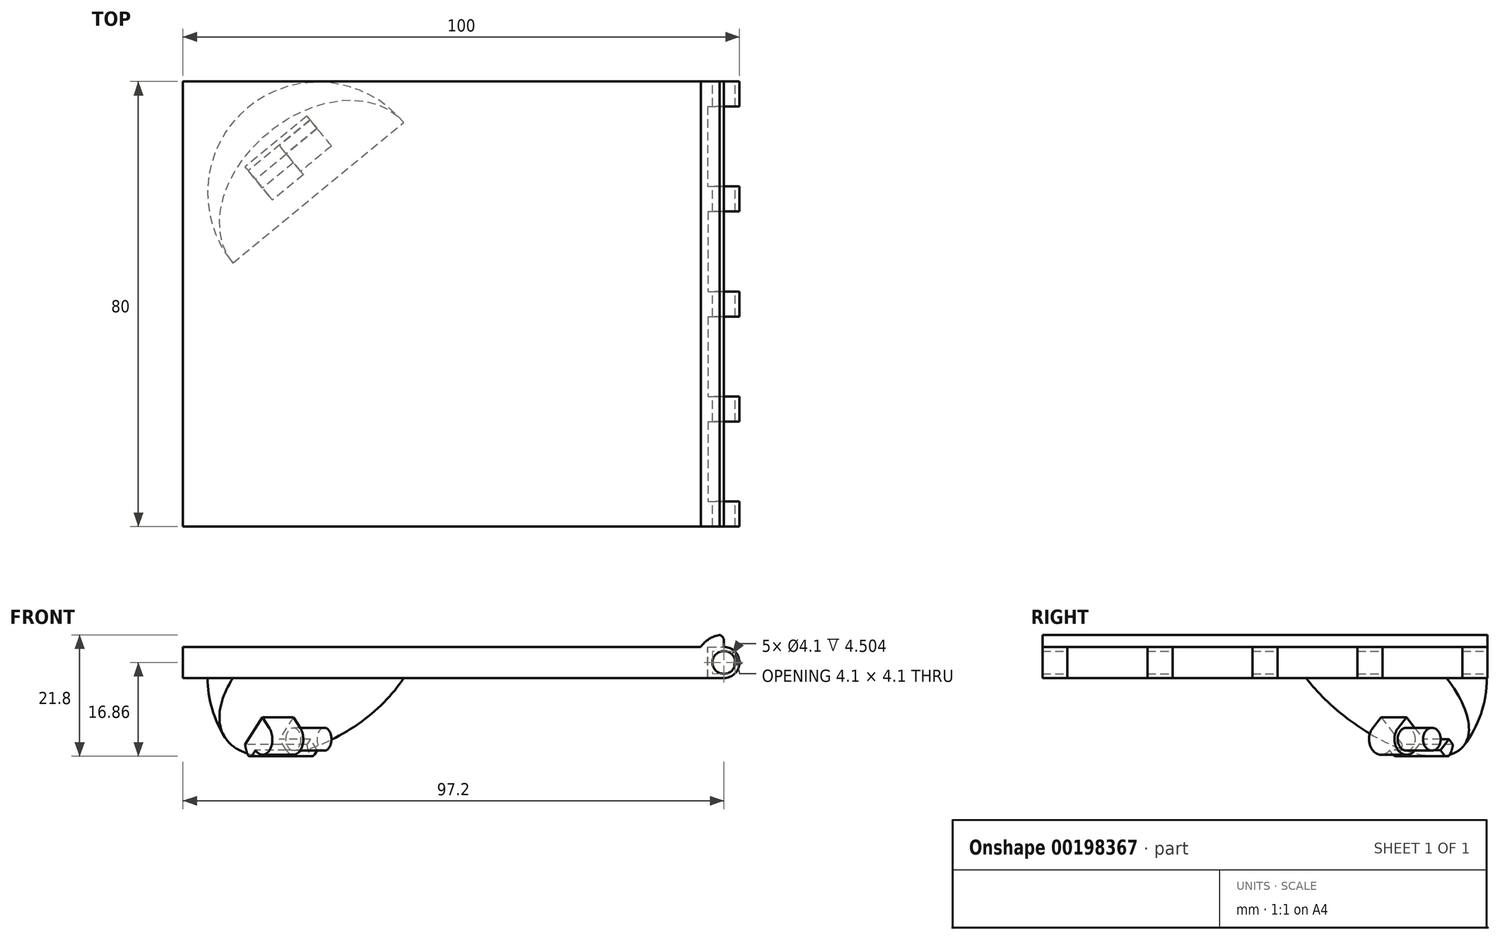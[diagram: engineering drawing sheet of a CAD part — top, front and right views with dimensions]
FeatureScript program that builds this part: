
annotation { "Feature Type Name" : "Feature", "Feature Type Description" : "" }
export const myFeature = defineFeature(function(context is Context, id is Id, definition is map)
    precondition{}
    {
        {
            var Q0;
            Q0=qCreatedBy(makeId("Front.planeOp"),FACE);
            var sketch = newSketch(context, id + "F0", { "sketchPlane" : qUnion([Q0])});
            skLineSegment(sketch, "E0.bottom", {"start": v(0, 0) * mm, "end": v(100, 0) * mm});
            skLineSegment(sketch, "E0.top", {"start": v(0, 5.6) * mm, "end": v(100, 5.6) * mm});
            skLineSegment(sketch, "E0.left", {"start": v(0, 0) * mm, "end": v(0, 5.6) * mm});
            skLineSegment(sketch, "E0.right", {"start": v(100, 0) * mm, "end": v(100, 5.6) * mm});
            skSolve(sketch);
        }
        {
            var Q0;
            Q0=makeQuery(id+"F0.imprint","IMPRINT",FACE,{"disambiguationData":[TD([[makeQuery(id+"F0.imprint","IMPRINT",EDGE,{"derivedFrom":sQuery(id+"F0.wireOp",EDGE,"E0.bottom")}),1.0]])]});
            extrude(context, id + "F1", {"entities" : qUnion([Q0]), "depth" : 80 * mm});
        }
        {
            var Q0;
            Q0=makeQuery(id+"F1.opExtrude","SWEPT_FACE",FACE,{"disambiguationData":[OSD([sQuery(id+"F0.wireOp",EDGE,"E0.top")])]});
            var sketch = newSketch(context, id + "F2", { "sketchPlane" : qUnion([Q0])});
            skLineSegment(sketch, "E1.bottom", {"start": v(100, 0) * mm, "end": v(94.3, 0) * mm, "construction": true});
            skLineSegment(sketch, "E1.top", {"start": v(100, -4.5) * mm, "end": v(94.3, -4.5) * mm, "construction": true});
            skLineSegment(sketch, "E1.left", {"start": v(100, 0) * mm, "end": v(100, -4.5) * mm, "construction": true});
            skLineSegment(sketch, "E1.right", {"start": v(94.3, 0) * mm, "end": v(94.3, -4.5) * mm, "construction": true});
            skLineSegment(sketch, "E2.bottom", {"start": v(94.3, -4.5) * mm, "end": v(100, -4.5) * mm});
            skLineSegment(sketch, "E2.top", {"start": v(94.3, -18.87) * mm, "end": v(100, -18.87) * mm});
            skLineSegment(sketch, "E2.left", {"start": v(94.3, -4.5) * mm, "end": v(94.3, -18.87) * mm});
            skLineSegment(sketch, "E2.right", {"start": v(100, -4.5) * mm, "end": v(100, -18.87) * mm});
            skLineSegment(sketch, "E3.0.1.0", {"start": v(100, -23.38) * mm, "end": v(100, -37.75) * mm});
            skLineSegment(sketch, "E3.0.1.1", {"start": v(100, -18.87) * mm, "end": v(94.3, -18.87) * mm, "construction": true});
            skLineSegment(sketch, "E3.0.1.2", {"start": v(94.3, -23.38) * mm, "end": v(94.3, -37.75) * mm});
            skLineSegment(sketch, "E3.0.1.3", {"start": v(94.3, -37.75) * mm, "end": v(100, -37.75) * mm});
            skLineSegment(sketch, "E3.0.1.4", {"start": v(100, -23.38) * mm, "end": v(94.3, -23.38) * mm, "construction": true});
            skLineSegment(sketch, "E3.0.1.5", {"start": v(100, -18.87) * mm, "end": v(100, -23.38) * mm, "construction": true});
            skLineSegment(sketch, "E3.0.1.6", {"start": v(94.3, -18.87) * mm, "end": v(94.3, -23.38) * mm, "construction": true});
            skLineSegment(sketch, "E3.0.1.7", {"start": v(94.3, -23.38) * mm, "end": v(100, -23.38) * mm});
            skLineSegment(sketch, "E3.0.2.0", {"start": v(100.02, -42.25) * mm, "end": v(100.02, -56.62) * mm});
            skLineSegment(sketch, "E3.0.2.1", {"start": v(100.02, -37.75) * mm, "end": v(94.32, -37.75) * mm, "construction": true});
            skLineSegment(sketch, "E3.0.2.2", {"start": v(94.32, -42.25) * mm, "end": v(94.32, -56.62) * mm});
            skLineSegment(sketch, "E3.0.2.3", {"start": v(94.32, -56.62) * mm, "end": v(100.02, -56.62) * mm});
            skLineSegment(sketch, "E3.0.2.4", {"start": v(100.02, -42.25) * mm, "end": v(94.32, -42.25) * mm, "construction": true});
            skLineSegment(sketch, "E3.0.2.5", {"start": v(100.02, -37.75) * mm, "end": v(100.02, -42.25) * mm, "construction": true});
            skLineSegment(sketch, "E3.0.2.6", {"start": v(94.32, -37.75) * mm, "end": v(94.32, -42.25) * mm, "construction": true});
            skLineSegment(sketch, "E3.0.2.7", {"start": v(94.32, -42.25) * mm, "end": v(100.02, -42.25) * mm});
            skLineSegment(sketch, "E3.0.3.0", {"start": v(100.03, -61.13) * mm, "end": v(100.03, -75.5) * mm});
            skLineSegment(sketch, "E3.0.3.1", {"start": v(100.03, -56.62) * mm, "end": v(94.33, -56.62) * mm, "construction": true});
            skLineSegment(sketch, "E3.0.3.2", {"start": v(94.33, -61.13) * mm, "end": v(94.33, -75.5) * mm});
            skLineSegment(sketch, "E3.0.3.3", {"start": v(94.33, -75.5) * mm, "end": v(100.03, -75.5) * mm});
            skLineSegment(sketch, "E3.0.3.4", {"start": v(100.03, -61.13) * mm, "end": v(94.33, -61.13) * mm, "construction": true});
            skLineSegment(sketch, "E3.0.3.5", {"start": v(100.03, -56.62) * mm, "end": v(100.03, -61.13) * mm, "construction": true});
            skLineSegment(sketch, "E3.0.3.6", {"start": v(94.33, -56.62) * mm, "end": v(94.33, -61.13) * mm, "construction": true});
            skLineSegment(sketch, "E3.0.3.7", {"start": v(94.33, -61.13) * mm, "end": v(100.03, -61.13) * mm});
            skLineSegment(sketch, "E3.direction1", {"start": v(94.3, -18.87) * mm, "end": v(119.7, -18.87) * mm, "construction": true});
            skLineSegment(sketch, "E3.direction2", {"start": v(94.3, -18.87) * mm, "end": v(94.3, -37.75) * mm, "construction": true});
            skSolve(sketch);
        }
        {
            var Q0;
            Q0=makeQuery(id+"F1.opExtrude","CAP_FACE",FACE,{"disambiguationData":[OSD([sQuery(id+"F0.wireOp",EDGE,"E0.bottom"),sQuery(id+"F0.wireOp",EDGE,"E0.top"),sQuery(id+"F0.wireOp",EDGE,"E0.left"),sQuery(id+"F0.wireOp",EDGE,"E0.right")])],"isStart":true});
            var sketch = newSketch(context, id + "F3", { "sketchPlane" : qUnion([Q0])});
            skLineSegment(sketch, "E4.bottom", {"start": v(-100, 5.6) * mm, "end": v(-94.4, 5.6) * mm, "construction": true});
            skLineSegment(sketch, "E4.top", {"start": v(-100, 0) * mm, "end": v(-94.4, 0) * mm, "construction": true});
            skLineSegment(sketch, "E4.left", {"start": v(-100, 5.6) * mm, "end": v(-100, 0) * mm, "construction": true});
            skLineSegment(sketch, "E4.right", {"start": v(-94.4, 5.6) * mm, "end": v(-94.4, 0) * mm, "construction": true});
            skLineSegment(sketch, "E5", {"start": v(-100, 5.6) * mm, "end": v(-94.4, 0) * mm, "construction": true});
            skCircle(sketch, "E6", {"center": v(-97.2, 2.8) * mm, "radius": 2.05 * mm});
            skLineSegment(sketch, "E7", {"start": v(-97.2, 2.8) * mm, "end": v(-97.2, 6.7) * mm, "construction": true});
            skLineSegment(sketch, "E8", {"start": v(-97.2, 6.7) * mm, "end": v(-97.2, 5.6) * mm});
            skCircle(sketch, "E9", {"center": v(-97.2, 6.7) * mm, "radius": 1.1 * mm, "construction": true});
            skArc(sketch, "E10", {"start": v(-96.45, 7.74) * mm, "mid": v(-97.19, 6.52) * mm, "end": v(-96.1, 5.6) * mm});
            skCircle(sketch, "E11", {"center": v(-97.2, 2.8) * mm, "radius": 2.8 * mm});
            skLineSegment(sketch, "E12", {"start": v(-97.2, 0) * mm, "end": v(-93.06, 0) * mm});
            skPoint(sketch, "E13.orphan", {"position": v(-97.2, 7.8) * mm});
            skLineSegment(sketch, "E14", {"start": v(-96.1, 5.6) * mm, "end": v(-93.06, 5.6) * mm});
            skLineSegment(sketch, "E15", {"start": v(-97.2, 5.6) * mm, "end": v(-100, 5.6) * mm});
            skLineSegment(sketch, "E16", {"start": v(-100, 5.6) * mm, "end": v(-100, 0) * mm});
            skLineSegment(sketch, "E17", {"start": v(-100, 0) * mm, "end": v(-97.2, 0) * mm});
            skCircle(sketch, "E18", {"center": v(-94.4, 2.8) * mm, "radius": 2.8 * mm, "construction": true});
            skLineSegment(sketch, "E19", {"start": v(-93.06, 0) * mm, "end": v(-91.6, 0) * mm});
            skArc(sketch, "E20.trimOffspring", {"start": v(-94.4, 2.8) * mm, "mid": v(-93.58, 0.82) * mm, "end": v(-91.6, 0) * mm});
            skArc(sketch, "E21.trimOffspring", {"start": v(-93.06, 5.6) * mm, "mid": v(-94.53, 7.03) * mm, "end": v(-96.45, 7.74) * mm});
            skLineSegment(sketch, "E22", {"start": v(-94.4, 2.8) * mm, "end": v(-94.4, 5.6) * mm});
            skSolve(sketch);
        }
        {
            var Q0;
            {var subQ0=sQuery(id+"F3.wireOp",EDGE,"E15");Q0=makeQuery(id+"F3.imprint","IMPRINT",FACE,{"disambiguationData":[TD([[makeQuery(id+"F3.imprint","IMPRINT",EDGE,{"derivedFrom":subQ0}),1.0]])]});}
            var Q1;
            {var subQ0=sQuery(id+"F3.wireOp",EDGE,"E17");Q1=makeQuery(id+"F3.imprint","IMPRINT",FACE,{"disambiguationData":[TD([[makeQuery(id+"F3.imprint","IMPRINT",EDGE,{"derivedFrom":subQ0}),-1.0]])]});}
            var Q2;
            Q2=makeQuery(id+"F3.imprint","IMPRINT",FACE,{"disambiguationData":[TD([[makeQuery(id+"F3.imprint","IMPRINT",EDGE,{"derivedFrom":sQuery(id+"F3.wireOp",EDGE,"E6")}),1.0]])]});
            extrude(context, id + "F4", {"entities" : qUnion([Q0, Q1, Q2]), "operationType" : NewBodyOperationType.REMOVE, "oppositeDirection" : true, "depth" : 80 * mm});
        }
        {
            var Q0;
            Q0=makeQuery(id+"F2.imprint","IMPRINT",FACE,{"disambiguationData":[TD([[makeQuery(id+"F2.imprint","IMPRINT",EDGE,{"derivedFrom":sQuery(id+"F2.wireOp",EDGE,"E2.bottom")}),-1.0]])]});
            var Q1;
            {var subQ0=sQuery(id+"F2.wireOp",EDGE,"E3.0.1.2");Q1=makeQuery(id+"F2.imprint","IMPRINT",FACE,{"disambiguationData":[TD([[makeQuery(id+"F2.imprint","IMPRINT",EDGE,{"derivedFrom":subQ0}),1.0]])]});}
            var Q2;
            {var subQ0=sQuery(id+"F2.wireOp",EDGE,"E3.0.2.2");Q2=makeQuery(id+"F2.imprint","IMPRINT",FACE,{"disambiguationData":[TD([[makeQuery(id+"F2.imprint","IMPRINT",EDGE,{"derivedFrom":subQ0}),1.0]])]});}
            var Q3;
            {var subQ0=sQuery(id+"F2.wireOp",EDGE,"E3.0.3.2");Q3=makeQuery(id+"F2.imprint","IMPRINT",FACE,{"disambiguationData":[TD([[makeQuery(id+"F2.imprint","IMPRINT",EDGE,{"derivedFrom":subQ0}),1.0]])]});}
            extrude(context, id + "F5", {"entities" : qUnion([Q0, Q1, Q2, Q3]), "operationType" : NewBodyOperationType.REMOVE, "oppositeDirection" : true, "depth" : 5.6 * mm});
        }
        {
            var Q0;
            {var subQ3=sQuery(id+"F3.wireOp",EDGE,"E14");Q0=makeQuery(id+"F3.imprint","IMPRINT",FACE,{"disambiguationData":[TD([[makeQuery(id+"F3.imprint","IMPRINT",EDGE,{"derivedFrom":subQ3}),-1.0]])]});}
            var Q1;
            {var subQ0=sQuery(id+"F3.wireOp",EDGE,"E8");Q1=makeQuery(id+"F3.imprint","IMPRINT",FACE,{"disambiguationData":[TD([[makeQuery(id+"F3.imprint","IMPRINT",EDGE,{"derivedFrom":subQ0}),1.0]])]});}
            extrude(context, id + "F6", {"entities" : qUnion([Q0, Q1]), "operationType" : NewBodyOperationType.ADD, "oppositeDirection" : true, "depth" : 80 * mm});
        }
        {
            var Q0;
            Q0=makeQuery(id+"F1.opExtrude","SWEPT_FACE",FACE,{"disambiguationData":[OSD([sQuery(id+"F0.wireOp",EDGE,"E0.bottom")])]});
            var sketch = newSketch(context, id + "F7", { "sketchPlane" : qUnion([Q0])});
            skLineSegment(sketch, "E23", {"start": v(0, 40) * mm, "end": v(97.2, 39.47) * mm, "construction": true});
            skLineSegment(sketch, "E24", {"start": v(48.6, 0) * mm, "end": v(48.6, 80) * mm, "construction": true});
            skLineSegment(sketch, "E25", {"start": v(0, 40) * mm, "end": v(48.6, 0) * mm, "construction": true});
            skCircle(sketch, "E26", {"center": v(24.3, 20) * mm, "radius": 19.87 * mm});
            skLineSegment(sketch, "E27", {"start": v(8.96, 32.63) * mm, "end": v(39.64, 7.37) * mm});
            skSolve(sketch);
        }
        {
            var Q0;
            {var subQ0=sQuery(id+"F7.wireOp",EDGE,"E27");Q0=makeQuery(id+"F7.imprint","IMPRINT",FACE,{"disambiguationData":[TD([[makeQuery(id+"F7.imprint","IMPRINT",EDGE,{"derivedFrom":subQ0}),-1.0]])]});}
            var Q1;
            Q1=sQuery(id+"F7.wireOp",EDGE,"E27");
            revolve(context, id + "F8", {"operationType" : NewBodyOperationType.ADD, "entities" : qUnion([Q0]), "axis" : qUnion([Q1]), "revolveType" : RevolveType.ONE_DIRECTION, "oppositeDirection" : true, "angle" : 45 * degree});
        }
        {
            var Q0;
            Q0=makeQuery(id+"F8.opRevolve","CAP_FACE",FACE,{"disambiguationData":[OSD([sQuery(id+"F7.wireOp",EDGE,"E26"),sQuery(id+"F7.wireOp",EDGE,"E27")])],"isStart":false});
            var sketch = newSketch(context, id + "F9", { "sketchPlane" : qUnion([Q0])});
            skLineSegment(sketch, "E28", {"start": v(16.22, 15.83) * mm, "end": v(6.22, -1.34) * mm, "construction": true});
            skLineSegment(sketch, "E29", {"start": v(11.22, 7.24) * mm, "end": v(5, 10.86) * mm});
            skLineSegment(sketch, "E30", {"start": v(11.22, 7.24) * mm, "end": v(17.43, 3.63) * mm});
            skLineSegment(sketch, "E31", {"start": v(17.43, 3.63) * mm, "end": v(14.61, -1.2) * mm});
            skLineSegment(sketch, "E32", {"start": v(5, 10.86) * mm, "end": v(2.2, 6.02) * mm});
            skLineSegment(sketch, "E33", {"start": v(14.61, -1.2) * mm, "end": v(2.2, 6.02) * mm});
            skLineSegment(sketch, "E34", {"start": v(11.22, 7.24) * mm, "end": v(8.4, 2.4) * mm});
            skSolve(sketch);
        }
        {
            var Q0;
            Q0=makeQuery(id+"F9.imprint","IMPRINT",FACE,{"disambiguationData":[TD([[makeQuery(id+"F9.imprint","IMPRINT",EDGE,{"derivedFrom":sQuery(id+"F9.wireOp",EDGE,"E29")}),1.0]])]});
            extrude(context, id + "F10", {"entities" : qUnion([Q0]), "operationType" : NewBodyOperationType.ADD, "depth" : 5.6 * mm});
        }
        {
            var Q0;
            Q0=makeQuery(id+"F10.opExtrude","SWEPT_FACE",FACE,{"disambiguationData":[OSD([sQuery(id+"F9.wireOp",EDGE,"E32")])]});
            var sketch = newSketch(context, id + "F11", { "sketchPlane" : qUnion([Q0])});
            skLineSegment(sketch, "E35", {"start": v(23.86, -7.02) * mm, "end": v(23.86, -14.94) * mm, "construction": true});
            skCircle(sketch, "E36", {"center": v(23.86, -10.98) * mm, "radius": 2.05 * mm});
            skArc(sketch, "E37", {"start": v(20.32, -14.52) * mm, "mid": v(27.65, -7.73) * mm, "end": v(19.83, -13.95) * mm});
            skLineSegment(sketch, "E38", {"start": v(23.86, -10.98) * mm, "end": v(21.88, -12.96) * mm, "construction": true});
            skLineSegment(sketch, "E39", {"start": v(18.86, -10.98) * mm, "end": v(23.86, -10.98) * mm, "construction": true});
            skLineSegment(sketch, "E40", {"start": v(21.88, -12.96) * mm, "end": v(20.32, -14.52) * mm, "construction": true});
            skCircle(sketch, "E41", {"center": v(21.1, -13.74) * mm, "radius": 1.1 * mm, "construction": true});
            skLineSegment(sketch, "E42", {"start": v(21.1, -13.74) * mm, "end": v(20.32, -12.96) * mm, "construction": true});
            skArc(sketch, "E43", {"start": v(19.83, -13.95) * mm, "mid": v(21.28, -12.43) * mm, "end": v(19.23, -12.87) * mm});
            skLineSegment(sketch, "E44", {"start": v(21.1, -13.74) * mm, "end": v(21.88, -12.96) * mm});
            skCircle(sketch, "E45", {"center": v(23.86, -10.98) * mm, "radius": 2.8 * mm});
            skLineSegment(sketch, "E46", {"start": v(18.86, -10.98) * mm, "end": v(19.9, -10.98) * mm});
            skLineSegment(sketch, "E47", {"start": v(19.9, -10.98) * mm, "end": v(21.88, -12.96) * mm});
            skSolve(sketch);
        }
        {
            var Q0;
            {var subQ0=sQuery(id+"F11.wireOp",EDGE,"E45");var subQ1=sQuery(id+"F9.wireOp",EDGE,"E32");var subQ4=makeQuery(id+"F10.opExtrude","CAP_EDGE",EDGE,{"disambiguationData":[OSD([subQ1])],"isStart":false});var subQ5=makeQuery(id+"F11.imprint","INTERSECT",VERTEX,{"derivedFrom":[subQ4,subQ0]});Q0=makeQuery(id+"F11.imprint","IMPRINT",FACE,{"disambiguationData":[TD([[makeQuery(id+"F11.imprint","IMPRINT",EDGE,{"disambiguationData":[TD([[subQ5,-1.0]])],"derivedFrom":subQ4}),-1.0]])]});}
            var Q1;
            {var subQ0=sQuery(id+"F11.wireOp",EDGE,"E45");var subQ1=sQuery(id+"F9.wireOp",EDGE,"E32");var subQ4=makeQuery(id+"F10.opExtrude","CAP_EDGE",EDGE,{"disambiguationData":[OSD([subQ1])],"isStart":false});var subQ5=makeQuery(id+"F11.imprint","INTERSECT",VERTEX,{"derivedFrom":[subQ4,subQ0]});Q1=makeQuery(id+"F11.imprint","IMPRINT",FACE,{"disambiguationData":[TD([[makeQuery(id+"F11.imprint","IMPRINT",EDGE,{"disambiguationData":[TD([[subQ5,-1.0]])],"derivedFrom":subQ0}),-1.0]])]});}
            extrude(context, id + "F12", {"entities" : qUnion([Q0, Q1]), "operationType" : NewBodyOperationType.REMOVE, "oppositeDirection" : true, "depth" : 7.18 * mm});
        }
        {
            var Q0;
            {var subQ0=sQuery(id+"F11.wireOp",EDGE,"E43");var subQ1=sQuery(id+"F11.wireOp",EDGE,"E37");var subQ2=makeQuery(id+"F11.imprint","INTERSECT",VERTEX,{"disambiguationData":[OD(0.0)],"derivedFrom":[subQ1,subQ0]});Q0=makeQuery(id+"F11.imprint","IMPRINT",FACE,{"disambiguationData":[TD([[makeQuery(id+"F11.imprint","IMPRINT",EDGE,{"disambiguationData":[TD([[subQ2,1.0]])],"derivedFrom":subQ1}),1.0]])]});}
            var Q1;
            {var subQ3=sQuery(id+"F11.wireOp",EDGE,"E46");Q1=makeQuery(id+"F11.imprint","IMPRINT",FACE,{"disambiguationData":[TD([[makeQuery(id+"F11.imprint","IMPRINT",EDGE,{"derivedFrom":subQ3}),-1.0]])]});}
            var Q2;
            {var subQ0=sQuery(id+"F11.wireOp",EDGE,"E44");Q2=makeQuery(id+"F11.imprint","IMPRINT",FACE,{"disambiguationData":[TD([[makeQuery(id+"F11.imprint","IMPRINT",EDGE,{"derivedFrom":subQ0}),1.0]])]});}
            var Q3;
            Q3=makeQuery(id+"F11.imprint","IMPRINT",FACE,{"disambiguationData":[TD([[makeQuery(id+"F11.imprint","IMPRINT",EDGE,{"derivedFrom":sQuery(id+"F11.wireOp",EDGE,"E36")}),1.0]])]});
            extrude(context, id + "F13", {"entities" : qUnion([Q0, Q1, Q2, Q3]), "operationType" : NewBodyOperationType.ADD, "oppositeDirection" : true, "depth" : 14.37 * mm});
        }
    });
